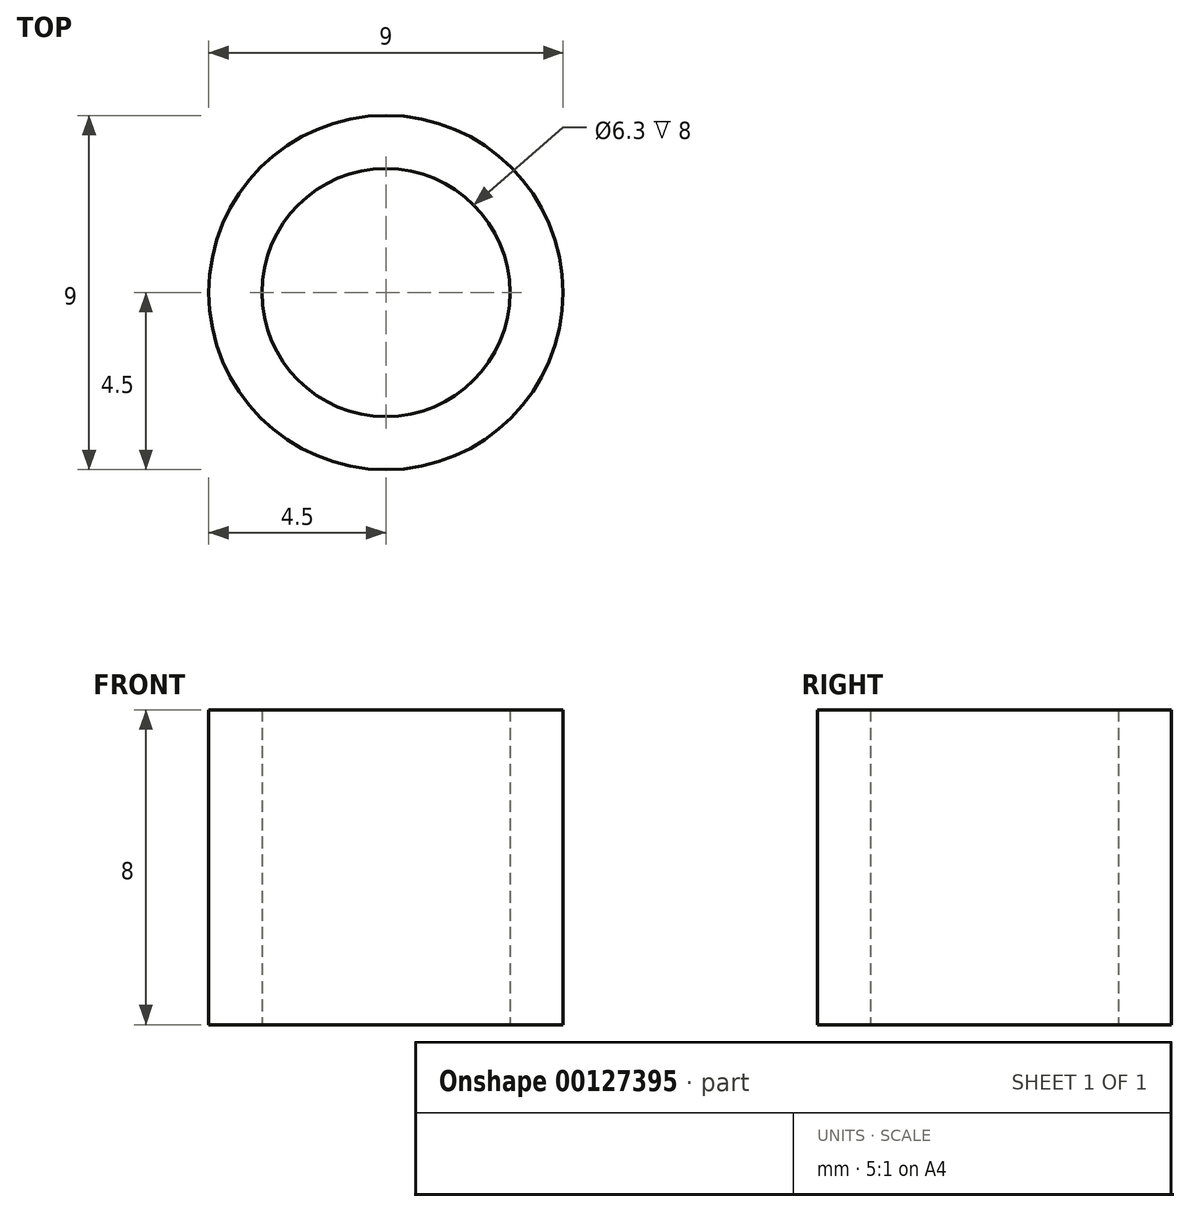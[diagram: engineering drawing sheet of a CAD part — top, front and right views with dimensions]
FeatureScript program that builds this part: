
annotation { "Feature Type Name" : "Feature", "Feature Type Description" : "" }
export const myFeature = defineFeature(function(context is Context, id is Id, definition is map)
    precondition{}
    {
        {
            var Q0;
            Q0=qCreatedBy(makeId("Top.planeOp"),FACE);
            var sketch = newSketch(context, id + "F0", { "sketchPlane" : qUnion([Q0])});
            skCircle(sketch, "E0", {"center": v(0, 0) * mm, "radius": 4.5 * mm});
            skCircle(sketch, "E1", {"center": v(0, 0) * mm, "radius": 3.15 * mm});
            skSolve(sketch);
        }
        {
            var Q0;
            Q0=makeQuery(id+"F0.imprint","IMPRINT",FACE,{"disambiguationData":[TD([[makeQuery(id+"F0.imprint","IMPRINT",EDGE,{"derivedFrom":sQuery(id+"F0.wireOp",EDGE,"E0")}),1.0]])]});
            extrude(context, id + "F1", {"entities" : qUnion([Q0]), "depth" : 8 * mm});
        }
    });
